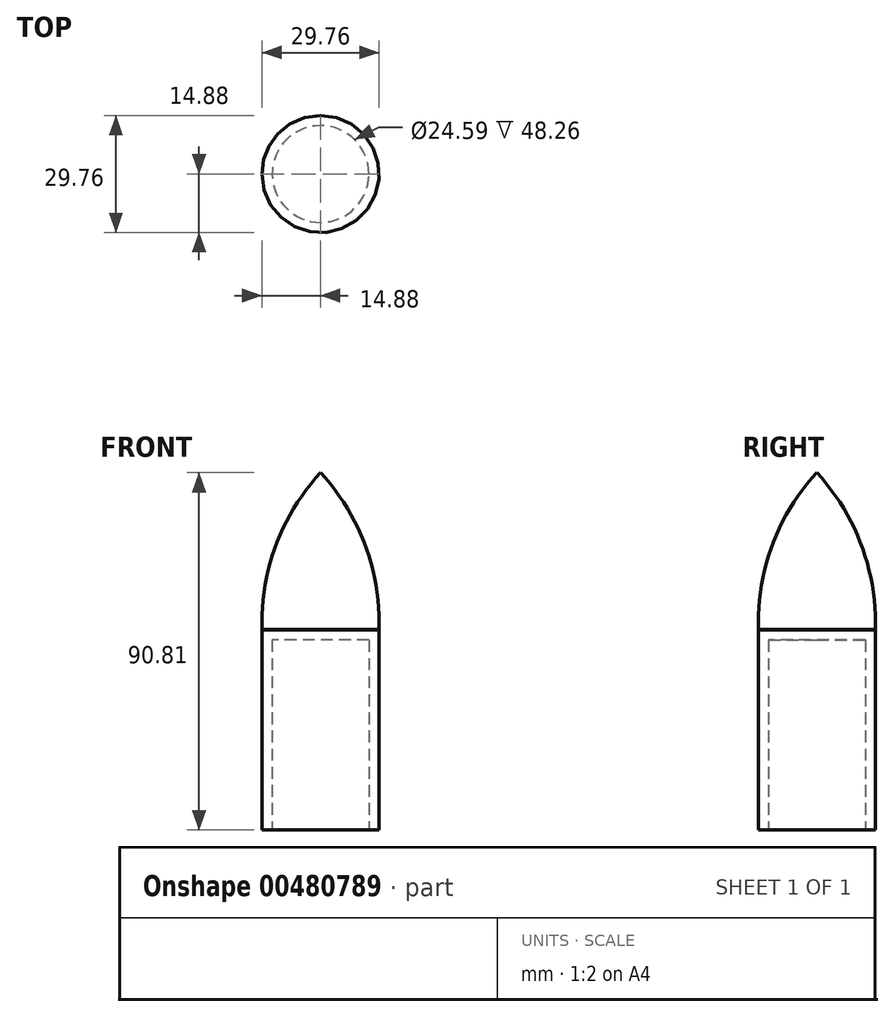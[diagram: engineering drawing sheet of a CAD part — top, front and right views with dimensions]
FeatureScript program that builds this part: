
annotation { "Feature Type Name" : "Feature", "Feature Type Description" : "" }
export const myFeature = defineFeature(function(context is Context, id is Id, definition is map)
    precondition{}
    {
        {
            var Q0;
            Q0=qCreatedBy(makeId("Top.planeOp"),FACE);
            var sketch = newSketch(context, id + "F0", { "sketchPlane" : qUnion([Q0])});
            skCircle(sketch, "E0", {"center": v(0, 0) * mm, "radius": 14.84 * mm});
            skSolve(sketch);
        }
        {
            var Q0;
            Q0 = qSketchRegion(id + "F0", true);
            extrude(context, id + "F1", {"entities" : qUnion([Q0]), "depth" : 50.8 * mm, "offsetDistance" : 25.4 * mm});
        }
        {
            var Q0;
            Q0=qCreatedBy(makeId("Right.planeOp"),FACE);
            var sketch = newSketch(context, id + "F2", { "sketchPlane" : qUnion([Q0])});
            skArc(sketch, "E1", {"start": v(0, 90.81) * mm, "mid": v(-11.36, 72.33) * mm, "end": v(-14.85, 50.92) * mm});
            skLineSegment(sketch, "E2", {"start": v(0, 90.81) * mm, "end": v(0, 52.03) * mm});
            skLineSegment(sketch, "E3", {"start": v(0, 52.03) * mm, "end": v(0, 50.92) * mm});
            skPoint(sketch, "E4.end.orphan", {"position": v(-14.85, 52.03) * mm});
            skLineSegment(sketch, "E5", {"start": v(0, 50.92) * mm, "end": v(-14.85, 50.92) * mm});
            skSolve(sketch);
        }
        {
            var Q0;
            Q0=makeQuery(id+"F2.imprint","IMPRINT",FACE,{"disambiguationData":[TD([[makeQuery(id+"F2.imprint","IMPRINT",EDGE,{"derivedFrom":sQuery(id+"F2.wireOp",EDGE,"E1")}),1.0]])]});
            var Q1;
            Q1=sQuery(id+"F2.wireOp",EDGE,"E2");
            revolve(context, id + "F3", {"surfaceOperationType" : NewSurfaceOperationType.NEW, "entities" : qUnion([Q0]), "axis" : qUnion([Q1]), "revolveType" : RevolveType.FULL});
        }
        {
            var Q0;
            Q0=makeQuery(id+"F1.opExtrude","CAP_FACE",FACE,{"disambiguationData":[OSD([sQuery(id+"F0.wireOp",EDGE,"E0")])],"isStart":true});
            shell(context, id + "F4", {"entities" : qUnion([Q0]), "thickness" : 2.54 * mm});
        }
    });
